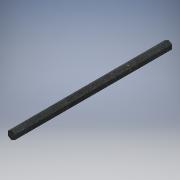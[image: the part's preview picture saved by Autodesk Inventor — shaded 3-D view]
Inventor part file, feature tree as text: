
AUTODESK INVENTOR PART (.ipt)
format: ipt  version: 2016 (Build 200138000, 138)  size: 96,768 bytes
history: native  units: in
note: dims shown in document units (in); Inventor stores cm internally (conversion verified against a paired STEP export)
features: extrude x1, sketch x1
ambient origin geometry x8: Origin, YZ Plane, XZ Plane, XY Plane, X Axis, Y Axis, Z Axis, Center Point
bodies: Solid1 (feature_tree)
feature tree (2):
  extrude  "Extrusion1"  Depth=8.0in TaperAngle=0.0deg
  sketch  "Sketch1"  dims[d0=0.375in d1=8.0in d2=0.0in]
